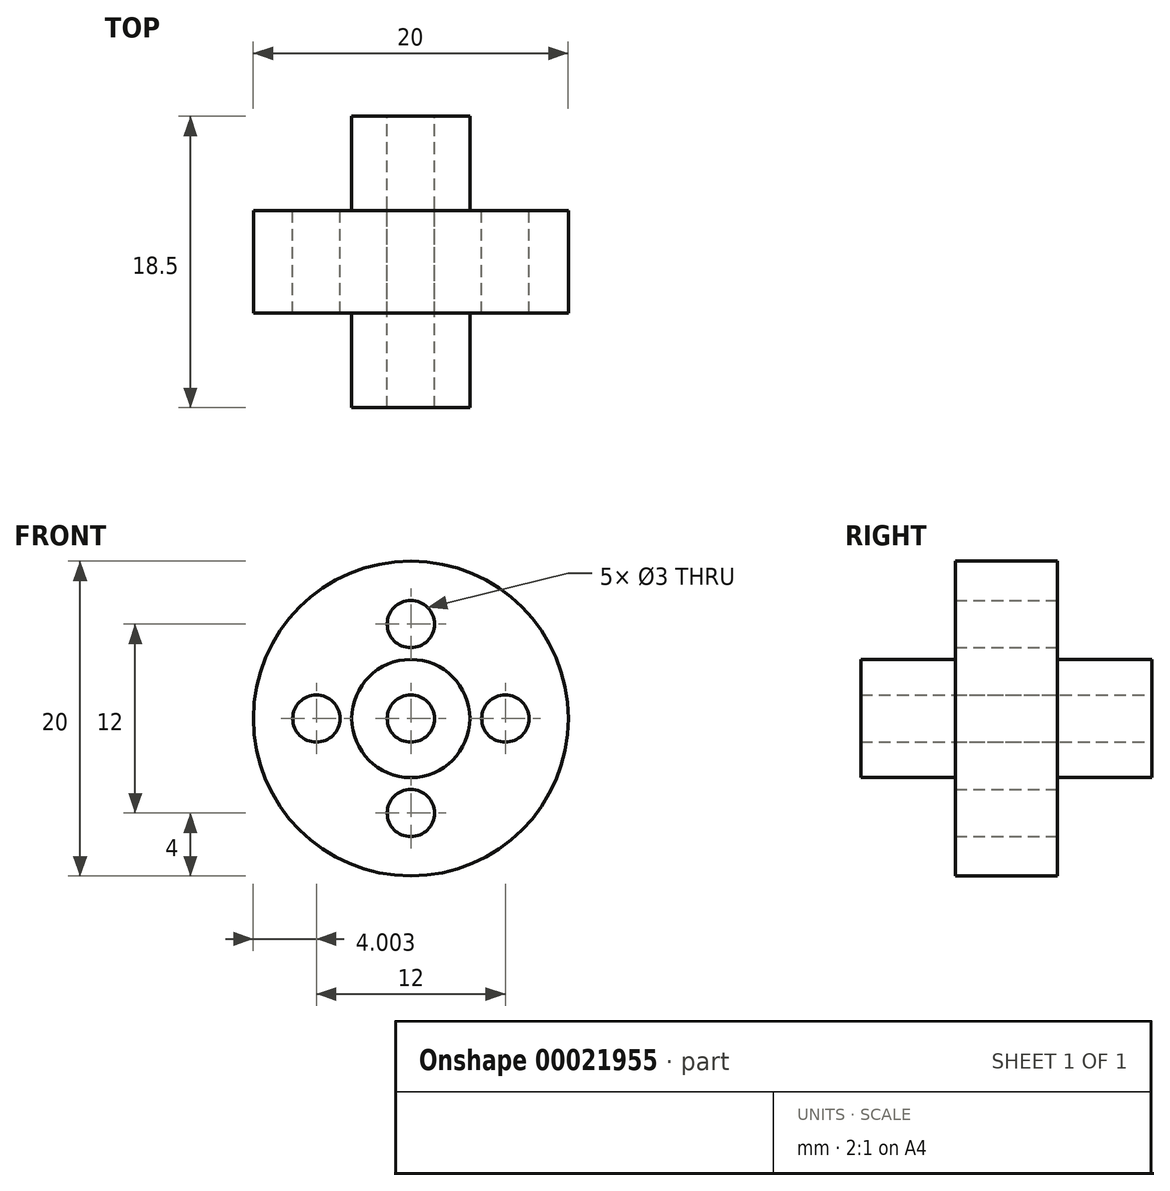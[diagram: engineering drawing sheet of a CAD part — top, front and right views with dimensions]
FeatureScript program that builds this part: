
annotation { "Feature Type Name" : "Feature", "Feature Type Description" : "" }
export const myFeature = defineFeature(function(context is Context, id is Id, definition is map)
    precondition{}
    {
        {
            var Q0;
            Q0=qCreatedBy(makeId("Front.planeOp"),FACE);
            var sketch = newSketch(context, id + "F0", { "sketchPlane" : qUnion([Q0])});
            skCircle(sketch, "E0", {"center": v(36.65, 26.67) * mm, "radius": 10 * mm});
            skCircle(sketch, "E1", {"center": v(36.65, 26.67) * mm, "radius": 1.5 * mm});
            skCircle(sketch, "E2", {"center": v(36.65, 26.67) * mm, "radius": 3.75 * mm});
            skLineSegment(sketch, "E3", {"start": v(36.65, 28.17) * mm, "end": v(36.65, 32.67) * mm});
            skCircle(sketch, "E4", {"center": v(36.65, 32.67) * mm, "radius": 1.5 * mm});
            skCircle(sketch, "E5.1.0", {"center": v(30.65, 26.67) * mm, "radius": 1.5 * mm});
            skCircle(sketch, "E5.2.0", {"center": v(36.65, 20.67) * mm, "radius": 1.5 * mm});
            skCircle(sketch, "E5.3.0", {"center": v(42.65, 26.67) * mm, "radius": 1.5 * mm});
            skSolve(sketch);
        }
        {
            var Q0;
            Q0 = qSketchRegion(id + "F0", true);
            extrude(context, id + "F1", {"entities" : qUnion([Q0]), "depth" : 6.5 * mm});
        }
        {
            var Q0;
            Q0=makeQuery(id+"F0.imprint","IMPRINT",FACE,{"disambiguationData":[TD([[makeQuery(id+"F0.imprint","IMPRINT",EDGE,{"derivedFrom":sQuery(id+"F0.wireOp",EDGE,"E1")}),-1.0]])]});
            extrude(context, id + "F2", {"entities" : qUnion([Q0]), "operationType" : NewBodyOperationType.ADD, "depth" : 12.5 * mm});
        }
        {
            var Q0;
            Q0=makeQuery(id+"F0.imprint","IMPRINT",FACE,{"disambiguationData":[TD([[makeQuery(id+"F0.imprint","IMPRINT",EDGE,{"derivedFrom":sQuery(id+"F0.wireOp",EDGE,"E1")}),-1.0]])]});
            extrude(context, id + "F3", {"entities" : qUnion([Q0]), "operationType" : NewBodyOperationType.ADD, "oppositeDirection" : true, "depth" : 6 * mm});
        }
    });
